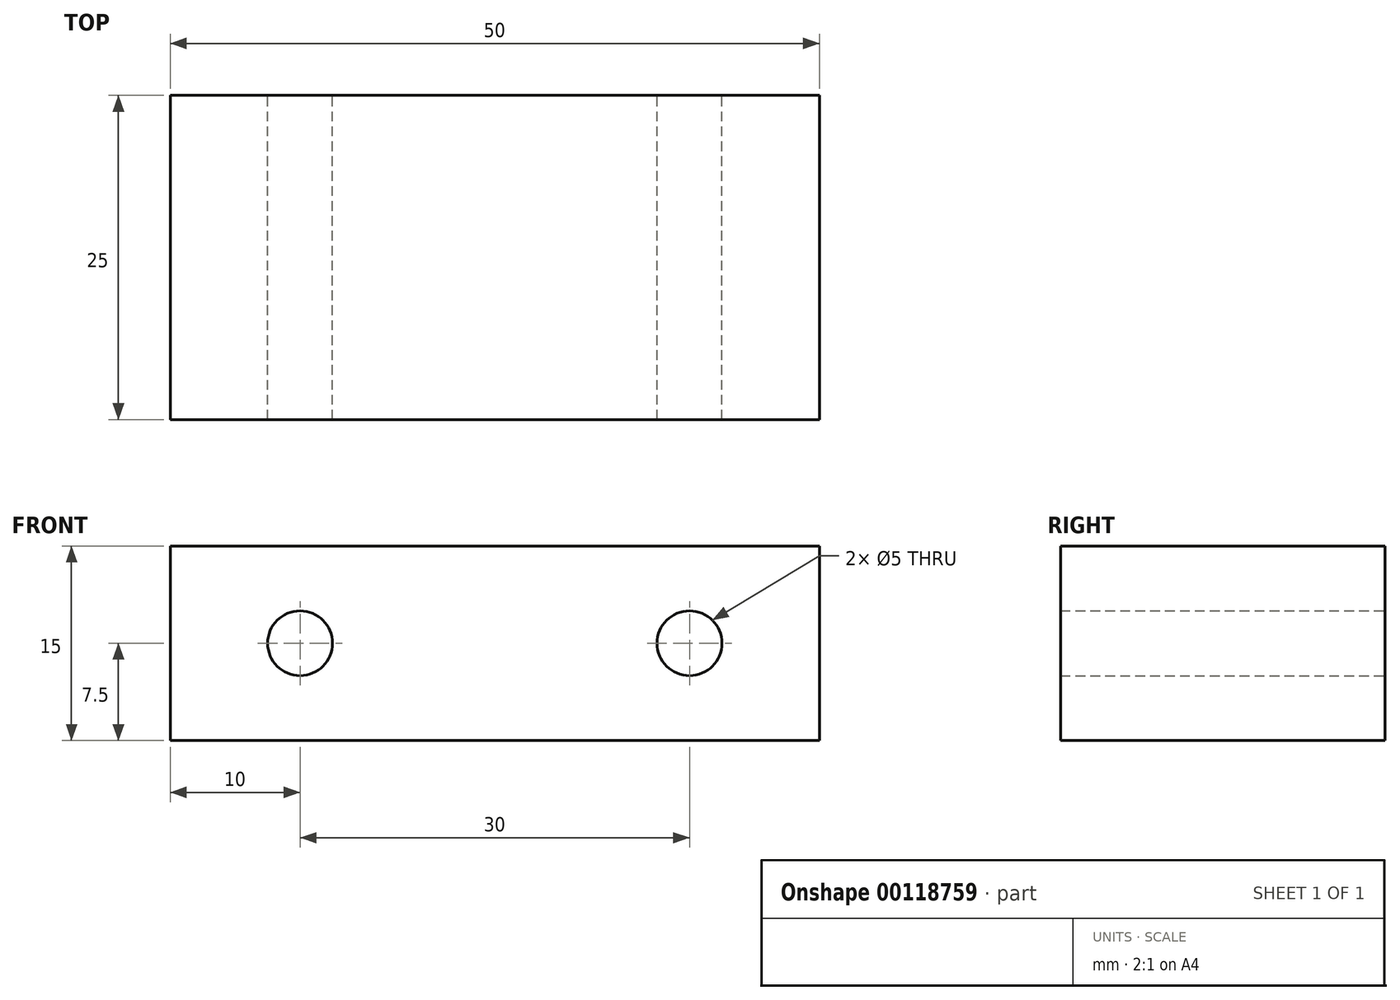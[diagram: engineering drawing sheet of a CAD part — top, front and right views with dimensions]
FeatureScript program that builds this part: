
annotation { "Feature Type Name" : "Feature", "Feature Type Description" : "" }
export const myFeature = defineFeature(function(context is Context, id is Id, definition is map)
    precondition{}
    {
        {
            var Q0;
            Q0=qCreatedBy(makeId("Front.planeOp"),FACE);
            var sketch = newSketch(context, id + "F0", { "sketchPlane" : qUnion([Q0])});
            skLineSegment(sketch, "E0.bottom", {"start": v(-25, 7.5) * mm, "end": v(25, 7.5) * mm});
            skLineSegment(sketch, "E0.top", {"start": v(-25, -7.5) * mm, "end": v(25, -7.5) * mm});
            skLineSegment(sketch, "E0.left", {"start": v(-25, 7.5) * mm, "end": v(-25, -7.5) * mm});
            skLineSegment(sketch, "E0.right", {"start": v(25, 7.5) * mm, "end": v(25, -7.5) * mm});
            skPoint(sketch, "E0.middle", {"position": v(0, 0) * mm});
            skPoint(sketch, "E1.endSnap0", {"position": v(-25, 0) * mm});
            skCircle(sketch, "E2", {"center": v(-15, 0) * mm, "radius": 2.5 * mm});
            skCircle(sketch, "E3", {"center": v(15, 0) * mm, "radius": 2.5 * mm});
            skSolve(sketch);
        }
        {
            var Q0;
            Q0=makeQuery(id+"F0.imprint","IMPRINT",FACE,{"disambiguationData":[TD([[makeQuery(id+"F0.imprint","IMPRINT",EDGE,{"derivedFrom":sQuery(id+"F0.wireOp",EDGE,"E0.bottom")}),-1.0]])]});
            extrude(context, id + "F1", {"entities" : qUnion([Q0]), "endBound" : BoundingType.SYMMETRIC, "depth" : 25 * mm});
        }
    });
